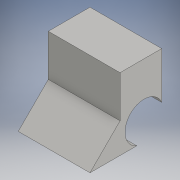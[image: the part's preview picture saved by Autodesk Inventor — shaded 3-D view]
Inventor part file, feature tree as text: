
AUTODESK INVENTOR PART (.ipt)
format: ipt  version: 2016 (Build 200138000, 138)  size: 90,624 bytes
history: native  units: in
note: dims shown in document units (in); Inventor stores cm internally (conversion verified against a paired STEP export)
features: extrude x1, sketch x1
ambient origin geometry x8: Origin, YZ Plane, XZ Plane, XY Plane, X Axis, Y Axis, Z Axis, Center Point
bodies: Solid1 (feature_tree)
feature tree (2):
  extrude  "Extrusion1"  Depth=3.937in
  sketch  "Sketch1"  dims[d2=3.937in d3=0.0in d5=2.1in]
